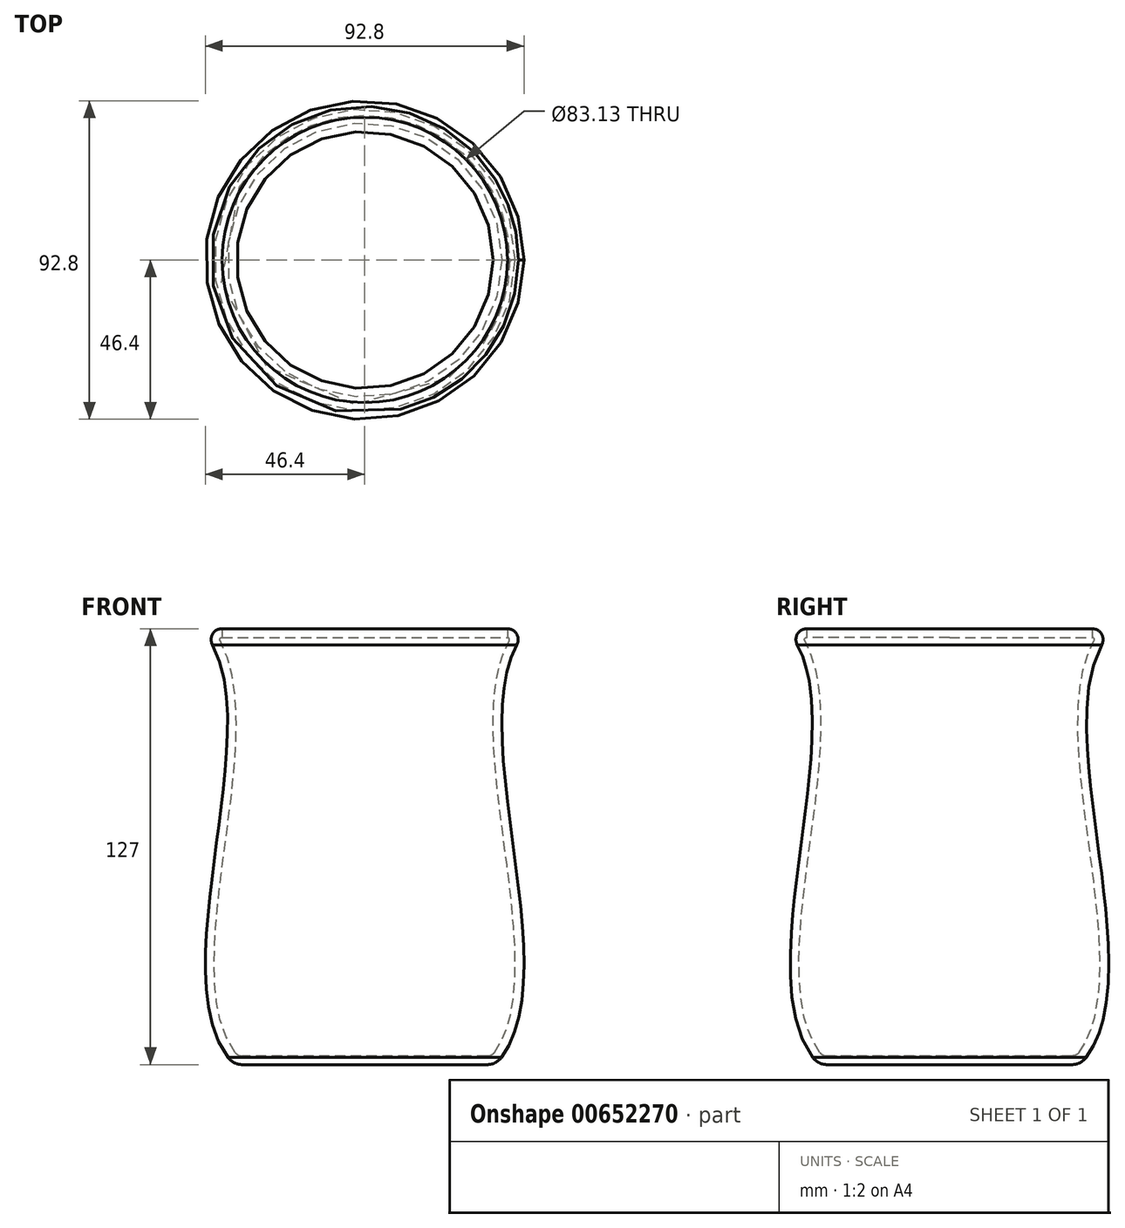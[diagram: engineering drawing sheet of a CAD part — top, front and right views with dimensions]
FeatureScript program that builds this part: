
annotation { "Feature Type Name" : "Feature", "Feature Type Description" : "" }
export const myFeature = defineFeature(function(context is Context, id is Id, definition is map)
    precondition{}
    {
        {
            var Q0;
            Q0=qCreatedBy(makeId("Front.planeOp"),FACE);
            var sketch = newSketch(context, id + "F0", { "sketchPlane" : qUnion([Q0])});
            skLineSegment(sketch, "E0", {"start": v(0, 0) * mm, "end": v(38.1, 0) * mm});
            skLineSegment(sketch, "E1", {"start": v(47.74, 127) * mm, "end": v(0, 127) * mm});
            skLineSegment(sketch, "E2", {"start": v(0, 127) * mm, "end": v(0, 0) * mm});
            skFitSpline(sketch, "E3", {"points": [v(38.1, 0) * mm, v(47.74, 127) * mm], "startDerivative": vector(70.96, 75.26) * mm, "endDerivative": vector(68.37, 71.92) * mm});
            skSolve(sketch);
        }
        {
            var Q0;
            Q0=makeQuery(id+"F0.imprint","IMPRINT",FACE,{"disambiguationData":[TD([[makeQuery(id+"F0.imprint","IMPRINT",EDGE,{"derivedFrom":sQuery(id+"F0.wireOp",EDGE,"E0")}),1.0]])]});
            var Q1;
            Q1=sQuery(id+"F0.wireOp",EDGE,"E2");
            revolve(context, id + "F1", {"entities" : qUnion([Q0]), "axis" : qUnion([Q1]), "revolveType" : RevolveType.FULL});
        }
        {
            var Q0;
            Q0=makeQuery(id+"F1.opRevolve","SWEPT_EDGE",EDGE,{"disambiguationData":[OSD([sQuery(id+"F0.wireOp",EDGE,"524adcd8-ece6-484a-b045-72bde1c73c7c"),sQuery(id+"F0.wireOp",EDGE,"E1")])]});
            fillet(context, id + "F2", {"entities" : qUnion([Q0]), "radius" : 3.17 * mm, "tangentPropagation" : true, "allowEdgeOverflow" : false});
        }
        {
            var Q0;
            Q0=makeQuery(id+"F1.opRevolve","SWEPT_EDGE",EDGE,{"disambiguationData":[OSD([sQuery(id+"F0.wireOp",EDGE,"E0"),sQuery(id+"F0.wireOp",EDGE,"524adcd8-ece6-484a-b045-72bde1c73c7c")])]});
            fillet(context, id + "F3", {"entities" : qUnion([Q0]), "radius" : 5.08 * mm, "tangentPropagation" : true, "allowEdgeOverflow" : false});
        }
        {
            var Q0;
            Q0=makeQuery(id+"F1.opRevolve","SWEPT_FACE",FACE,{"disambiguationData":[OSD([sQuery(id+"F0.wireOp",EDGE,"E1")])]});
            shell(context, id + "F4", {"entities" : qUnion([Q0]), "thickness" : 2.54 * mm});
        }
    });
